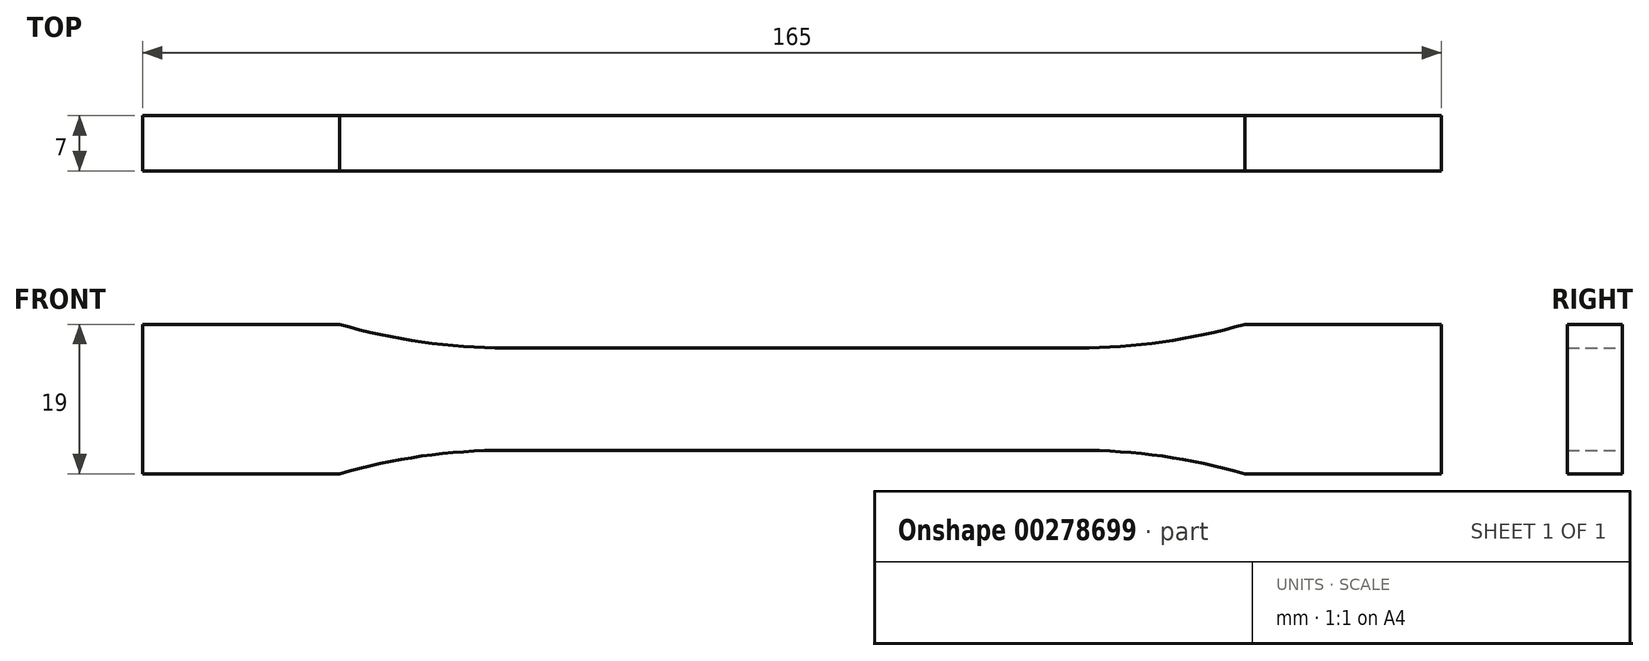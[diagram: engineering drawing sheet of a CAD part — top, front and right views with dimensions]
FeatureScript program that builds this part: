
annotation { "Feature Type Name" : "Feature", "Feature Type Description" : "" }
export const myFeature = defineFeature(function(context is Context, id is Id, definition is map)
    precondition{}
    {
        {
            var Q0;
            Q0=qCreatedBy(makeId("Front.planeOp"),FACE);
            var sketch = newSketch(context, id + "F0", { "sketchPlane" : qUnion([Q0])});
            skLineSegment(sketch, "E0", {"start": v(0, 6.5) * mm, "end": v(36.36, 6.5) * mm});
            skArc(sketch, "E1", {"start": v(36.36, 6.5) * mm, "mid": v(47.03, 7.25) * mm, "end": v(57.5, 9.5) * mm});
            skLineSegment(sketch, "E2", {"start": v(57.5, 9.5) * mm, "end": v(82.5, 9.5) * mm});
            skArc(sketch, "E3.MirrorCS", {"start": v(36.36, -6.5) * mm, "mid": v(47.03, -7.25) * mm, "end": v(57.5, -9.5) * mm});
            skLineSegment(sketch, "E4.MirrorCS", {"start": v(57.5, -9.5) * mm, "end": v(82.5, -9.5) * mm});
            skLineSegment(sketch, "E5.MirrorCS", {"start": v(0, -6.5) * mm, "end": v(36.36, -6.5) * mm});
            skLineSegment(sketch, "E6.MirrorCS", {"start": v(0, 6.5) * mm, "end": v(-36.36, 6.5) * mm});
            skLineSegment(sketch, "E7.MirrorCS", {"start": v(0, -6.5) * mm, "end": v(-36.36, -6.5) * mm});
            skArc(sketch, "E8.MirrorCS", {"start": v(-36.36, 6.5) * mm, "mid": v(-47.03, 7.25) * mm, "end": v(-57.5, 9.5) * mm});
            skLineSegment(sketch, "E9.MirrorCS", {"start": v(-57.5, -9.5) * mm, "end": v(-82.5, -9.5) * mm});
            skArc(sketch, "E10.MirrorCS", {"start": v(-36.36, -6.5) * mm, "mid": v(-47.03, -7.25) * mm, "end": v(-57.5, -9.5) * mm});
            skLineSegment(sketch, "E11.MirrorCS", {"start": v(-57.5, 9.5) * mm, "end": v(-82.5, 9.5) * mm});
            skLineSegment(sketch, "E12", {"start": v(-82.5, 9.5) * mm, "end": v(-82.5, -9.5) * mm});
            skLineSegment(sketch, "E13", {"start": v(82.5, 9.5) * mm, "end": v(82.5, -9.5) * mm});
            skSolve(sketch);
        }
        {
            var Q0;
            Q0=makeQuery(id+"F0.imprint","IMPRINT",FACE,{"disambiguationData":[TD([[makeQuery(id+"F0.imprint","IMPRINT",EDGE,{"derivedFrom":sQuery(id+"F0.wireOp",EDGE,"E5.MirrorCS")}),1.0]])]});
            extrude(context, id + "F1", {"entities" : qUnion([Q0]), "endBound" : BoundingType.SYMMETRIC, "depth" : 7 * mm});
        }
    });
